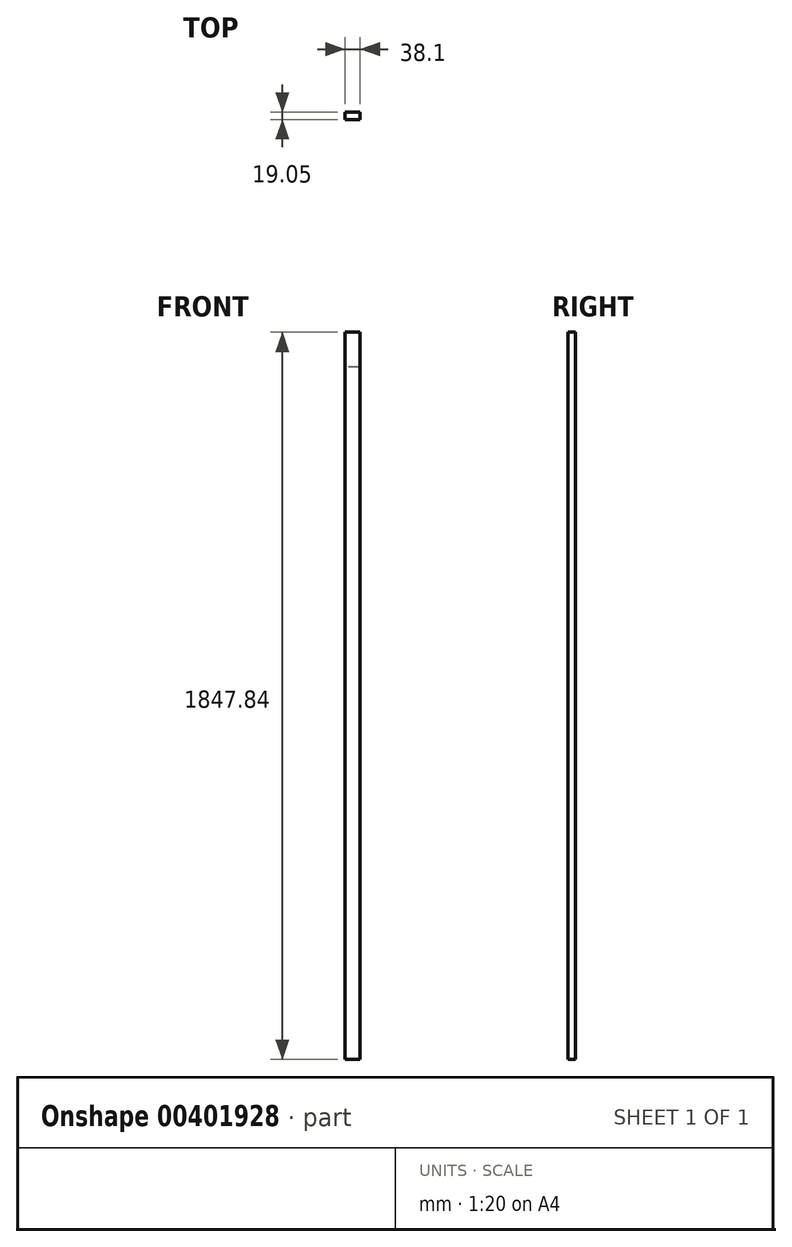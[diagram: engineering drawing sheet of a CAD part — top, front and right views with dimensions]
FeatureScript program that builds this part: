
annotation { "Feature Type Name" : "Feature", "Feature Type Description" : "" }
export const myFeature = defineFeature(function(context is Context, id is Id, definition is map)
    precondition{}
    {
        {
            var Q0;
            Q0=qCreatedBy(makeId("Front.planeOp"),FACE);
            var sketch = newSketch(context, id + "F0", { "sketchPlane" : qUnion([Q0])});
            skLineSegment(sketch, "E0.bottom", {"start": v(19.05, 923.93) * mm, "end": v(-19.05, 923.93) * mm});
            skLineSegment(sketch, "E0.top", {"start": v(19.05, -923.93) * mm, "end": v(-19.05, -923.93) * mm});
            skLineSegment(sketch, "E0.left", {"start": v(19.05, 923.93) * mm, "end": v(19.05, -923.93) * mm});
            skLineSegment(sketch, "E0.right", {"start": v(-19.05, 923.93) * mm, "end": v(-19.05, -923.93) * mm});
            skPoint(sketch, "E0.middle", {"position": v(0, 0) * mm});
            skSolve(sketch);
        }
        {
            var Q0;
            Q0=qSketchRegion(id+"F0",true);
            extrude(context, id + "F1", {"entities" : qUnion([Q0]), "depth" : 19.05 * mm});
        }
        {
            var Q0;
            Q0=makeQuery(id+"F1.opExtrude","CAP_FACE",FACE,{"disambiguationData":[OSD([sQuery(id+"F0.wireOp",EDGE,"E0.bottom"),sQuery(id+"F0.wireOp",EDGE,"E0.top"),sQuery(id+"F0.wireOp",EDGE,"E0.left"),sQuery(id+"F0.wireOp",EDGE,"E0.right")])],"isStart":true});
            var sketch = newSketch(context, id + "F2", { "sketchPlane" : qUnion([Q0])});
            skLineSegment(sketch, "E1.bottom", {"start": v(-19.05, 923.93) * mm, "end": v(19.05, 923.93) * mm});
            skLineSegment(sketch, "E1.top", {"start": v(-19.05, 835.03) * mm, "end": v(19.05, 835.03) * mm});
            skLineSegment(sketch, "E1.left", {"start": v(-19.05, 923.93) * mm, "end": v(-19.05, 835.03) * mm});
            skLineSegment(sketch, "E1.right", {"start": v(19.05, 923.93) * mm, "end": v(19.05, 835.03) * mm});
            skSolve(sketch);
        }
        {
            var Q0;
            Q0=qSketchRegion(id+"F2",true);
            extrude(context, id + "F3", {"entities" : qUnion([Q0]), "operationType" : NewBodyOperationType.REMOVE, "oppositeDirection" : true, "depth" : ((3 / 4) / 2) * mm});
        }
    });
